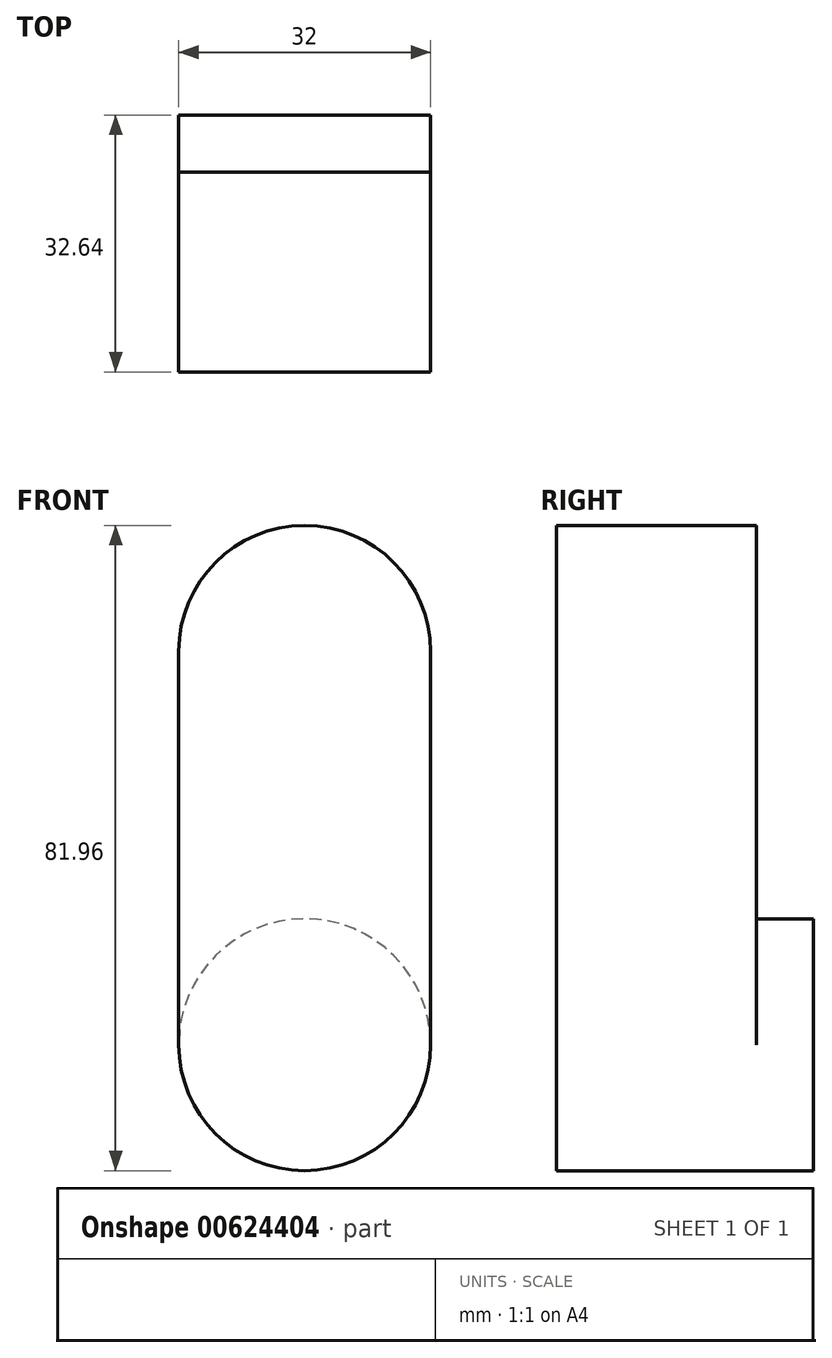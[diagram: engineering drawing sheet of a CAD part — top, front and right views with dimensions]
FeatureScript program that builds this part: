
annotation { "Feature Type Name" : "Feature", "Feature Type Description" : "" }
export const myFeature = defineFeature(function(context is Context, id is Id, definition is map)
    precondition{}
    {
        {
            var Q0;
            Q0=qCreatedBy(makeId("Front.planeOp"),FACE);
            var sketch = newSketch(context, id + "F0", { "sketchPlane" : qUnion([Q0])});
            skCircle(sketch, "E0", {"center": v(0, 0) * mm, "radius": 16 * mm});
            skCircle(sketch, "E1", {"center": v(0, -49.96) * mm, "radius": 16 * mm});
            skLineSegment(sketch, "E2", {"start": v(-16, 0) * mm, "end": v(-16, -49.96) * mm});
            skLineSegment(sketch, "E3", {"start": v(16, 0) * mm, "end": v(16, -49.96) * mm});
            skSolve(sketch);
        }
        {
            var Q0;
            {var subQ0=sQuery(id+"F0.wireOp",EDGE,"56NtTcvt-0Ff3-4Q8S-PygW-xFDhcGVLsMLW");var subQ1=sQuery(id+"F0.wireOp",EDGE,"E1");var subQ2=makeQuery(id+"F0.imprint","INTERSECT",VERTEX,{"disambiguationData":[OD(0.0)],"derivedFrom":[subQ1,subQ0]});Q0=makeQuery(id+"F0.imprint","IMPRINT",FACE,{"disambiguationData":[TD([[makeQuery(id+"F0.imprint","IMPRINT",EDGE,{"disambiguationData":[TD([[subQ2,-1.0]])],"derivedFrom":subQ1}),1.0]])]});}
            var Q1;
            {var subQ0=sQuery(id+"F0.wireOp",EDGE,"Tqyg4G9K-4kEb-3uDV-J0lA-mMjT9BIv1jDK");Q1=makeQuery(id+"F0.imprint","IMPRINT",FACE,{"disambiguationData":[TD([[makeQuery(id+"F0.imprint","IMPRINT",EDGE,{"derivedFrom":subQ0}),1.0]])]});}
            var Q2;
            {var subQ0=sQuery(id+"F0.wireOp",EDGE,"E1");var subQ1=makeQuery(id+"F0.imprint","INTERSECT",VERTEX,{"derivedFrom":[subQ0,sQuery(id+"F0.wireOp",EDGE,"Tqyg4G9K-4kEb-3uDV-J0lA-mMjT9BIv1jDK")]});Q2=makeQuery(id+"F0.imprint","IMPRINT",FACE,{"disambiguationData":[TD([[makeQuery(id+"F0.imprint","IMPRINT",EDGE,{"disambiguationData":[TD([[subQ1,1.0]])],"derivedFrom":subQ0}),1.0]])]});}
            extrude(context, id + "F1", {"entities" : qUnion([Q0, Q1, Q2]), "oppositeDirection" : true, "depth" : 7.24 * mm, "offsetDistance" : 25.4 * mm});
        }
        {
            var Q0;
            Q0 = qSketchRegion(id + "F0", true);
            extrude(context, id + "F2", {"entities" : qUnion([Q0]), "operationType" : NewBodyOperationType.ADD, "depth" : 25.4 * mm, "offsetDistance" : 25.4 * mm});
        }
    });
